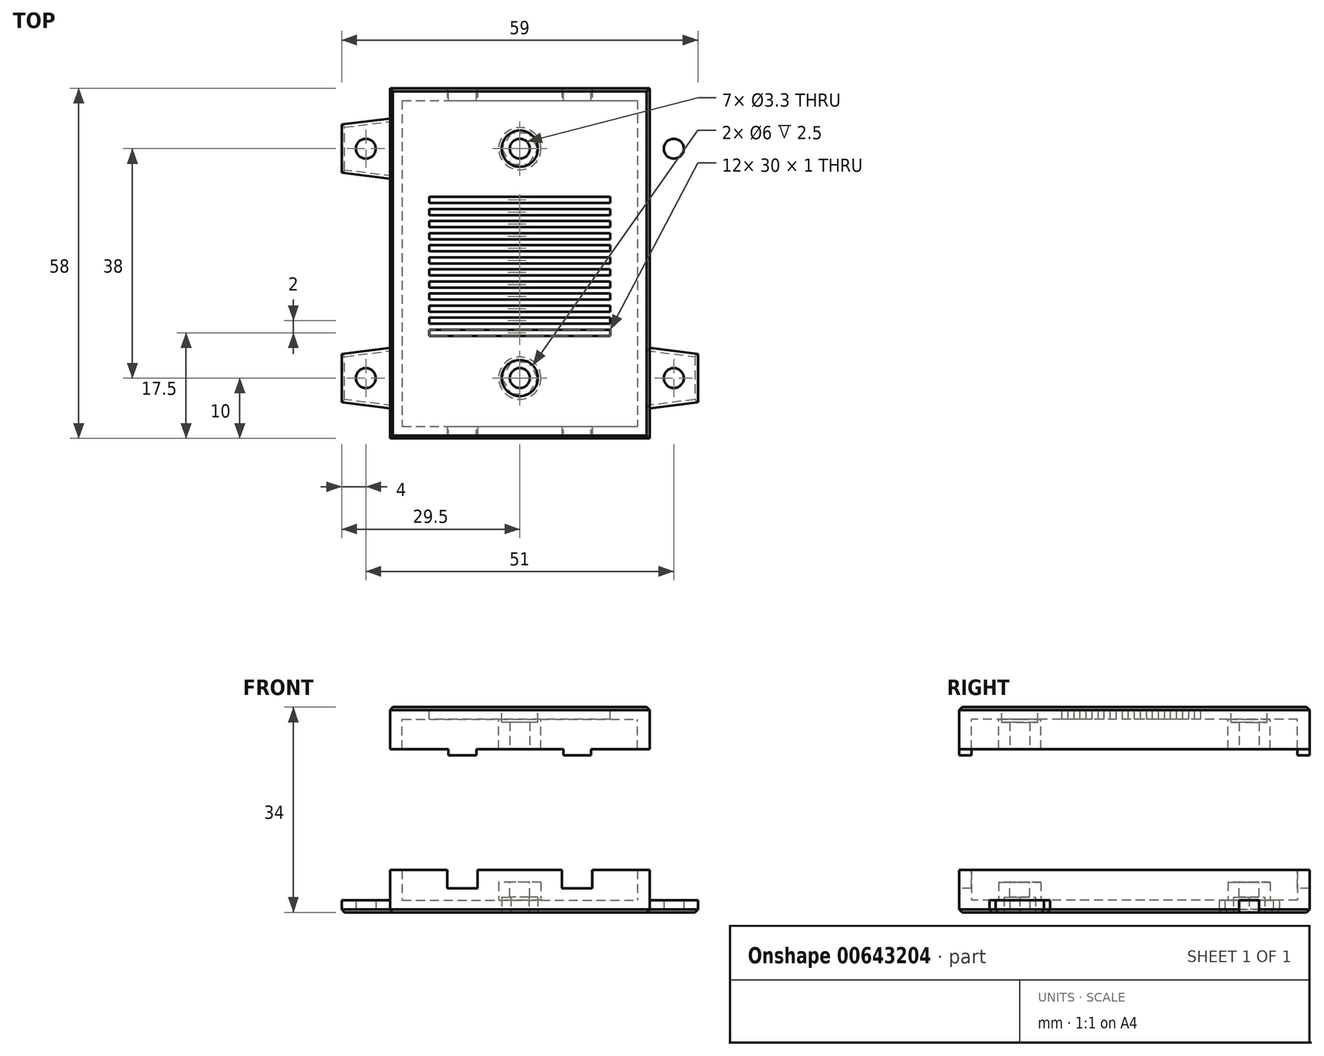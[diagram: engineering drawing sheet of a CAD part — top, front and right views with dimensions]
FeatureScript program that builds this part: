
annotation { "Feature Type Name" : "Feature", "Feature Type Description" : "" }
export const myFeature = defineFeature(function(context is Context, id is Id, definition is map)
    precondition{}
    {
        {
            var Q0;
            Q0=qCreatedBy(makeId("Top.planeOp"),FACE);
            var sketch = newSketch(context, id + "F0", { "sketchPlane" : qUnion([Q0])});
            skPoint(sketch, "E0", {"position": v(-9.5, 0) * mm});
            skPoint(sketch, "E1", {"position": v(0, -38) * mm});
            skPoint(sketch, "E2", {"position": v(0, 0) * mm});
            skPoint(sketch, "E3", {"position": v(9.5, 0) * mm});
            skLineSegment(sketch, "E4.bottom", {"start": v(-17.5, 6) * mm, "end": v(17.5, 6) * mm});
            skLineSegment(sketch, "E4.top", {"start": v(-17.5, -44) * mm, "end": v(17.5, -44) * mm});
            skLineSegment(sketch, "E4.left", {"start": v(-17.5, 6) * mm, "end": v(-17.5, -44) * mm});
            skLineSegment(sketch, "E4.right", {"start": v(17.5, 6) * mm, "end": v(17.5, -44) * mm});
            skPoint(sketch, "E5", {"position": v(-9.5, -38) * mm});
            skPoint(sketch, "E6", {"position": v(9.5, -38) * mm});
            skLineSegment(sketch, "E7.0", {"start": v(-19.5, -46) * mm, "end": v(19.5, -46) * mm});
            skLineSegment(sketch, "E7.1", {"start": v(-19.5, 8) * mm, "end": v(-19.5, -46) * mm});
            skLineSegment(sketch, "E7.2", {"start": v(-19.5, 8) * mm, "end": v(19.5, 8) * mm});
            skLineSegment(sketch, "E7.3", {"start": v(19.5, 8) * mm, "end": v(19.5, -46) * mm});
            skLineSegment(sketch, "E8.0", {"start": v(-21.5, -48) * mm, "end": v(21.5, -48) * mm});
            skLineSegment(sketch, "E8.1", {"start": v(-21.5, 10) * mm, "end": v(-21.5, -48) * mm});
            skLineSegment(sketch, "E8.2", {"start": v(-21.5, 10) * mm, "end": v(21.5, 10) * mm});
            skLineSegment(sketch, "E8.3", {"start": v(21.5, 10) * mm, "end": v(21.5, -48) * mm});
            skCircle(sketch, "E9", {"center": v(0, 0) * mm, "radius": 3.5 * mm});
            skCircle(sketch, "E10", {"center": v(0, -38) * mm, "radius": 3.5 * mm});
            skSolve(sketch);
        }
        {
            var Q0;
            Q0=makeQuery(id+"F0.imprint","IMPRINT",FACE,{"disambiguationData":[TD([[makeQuery(id+"F0.imprint","IMPRINT",EDGE,{"derivedFrom":sQuery(id+"F0.wireOp",EDGE,"E7.0")}),-1.0]])]});
            var Q1;
            Q1=makeQuery(id+"F0.imprint","IMPRINT",FACE,{"disambiguationData":[TD([[makeQuery(id+"F0.imprint","IMPRINT",EDGE,{"derivedFrom":sQuery(id+"F0.wireOp",EDGE,"E4.bottom")}),1.0]])]});
            var Q2;
            Q2=makeQuery(id+"F0.imprint","IMPRINT",FACE,{"disambiguationData":[TD([[makeQuery(id+"F0.imprint","IMPRINT",EDGE,{"derivedFrom":sQuery(id+"F0.wireOp",EDGE,"E4.bottom")}),-1.0]])]});
            var Q3;
            Q3=makeQuery(id+"F0.imprint","IMPRINT",FACE,{"disambiguationData":[TD([[makeQuery(id+"F0.imprint","IMPRINT",EDGE,{"derivedFrom":sQuery(id+"F0.wireOp",EDGE,"E9")}),1.0]])]});
            var Q4;
            Q4=makeQuery(id+"F0.imprint","IMPRINT",FACE,{"disambiguationData":[TD([[makeQuery(id+"F0.imprint","IMPRINT",EDGE,{"derivedFrom":sQuery(id+"F0.wireOp",EDGE,"E10")}),1.0]])]});
            extrude(context, id + "F1", {"entities" : qUnion([Q0, Q1, Q2, Q3, Q4]), "depth" : -2 * mm, "offsetDistance" : 25 * mm});
        }
        {
            var Q0;
            Q0=makeQuery(id+"F0.imprint","IMPRINT",FACE,{"disambiguationData":[TD([[makeQuery(id+"F0.imprint","IMPRINT",EDGE,{"derivedFrom":sQuery(id+"F0.wireOp",EDGE,"E7.0")}),-1.0]])]});
            extrude(context, id + "F2", {"entities" : qUnion([Q0]), "operationType" : NewBodyOperationType.ADD, "depth" : 5 * mm, "offsetDistance" : 25 * mm});
        }
        {
            var Q0;
            Q0=makeQuery(id+"F0.imprint","IMPRINT",FACE,{"disambiguationData":[TD([[makeQuery(id+"F0.imprint","IMPRINT",EDGE,{"derivedFrom":sQuery(id+"F0.wireOp",EDGE,"E9")}),1.0]])]});
            var Q1;
            Q1=makeQuery(id+"F0.imprint","IMPRINT",FACE,{"disambiguationData":[TD([[makeQuery(id+"F0.imprint","IMPRINT",EDGE,{"derivedFrom":sQuery(id+"F0.wireOp",EDGE,"E10")}),1.0]])]});
            extrude(context, id + "F3", {"entities" : qUnion([Q0, Q1]), "operationType" : NewBodyOperationType.ADD, "depth" : 3 * mm, "offsetDistance" : 25 * mm});
        }
        {
            var Q0;
            Q0=makeQuery(id+"F3.opExtrude","CAP_FACE",FACE,{"disambiguationData":[OSD([sQuery(id+"F0.wireOp",EDGE,"E9")])],"isStart":false});
            var sketch = newSketch(context, id + "F4", { "sketchPlane" : qUnion([Q0])});
            skPoint(sketch, "E11", {"position": v(0, 0) * mm});
            skCircle(sketch, "E12.0", {"center": v(0, -38) * mm, "radius": 3.5 * mm});
            skCircle(sketch, "E13.0", {"center": v(0, 0) * mm, "radius": 3.5 * mm});
            skSolve(sketch);
        }
        {
            var Q0;
            Q0=sQuery(id+"F4.wireOp",VERTEX,"E12.0.center");
            var Q1;
            Q1=sQuery(id+"F4.wireOp",VERTEX,"E11");
            var Q2;
            Q2=makeQuery(id+"F1.opExtrude","SWEPT_BODY",BODY,{"disambiguationData":[OSD([sQuery(id+"F0.wireOp",EDGE,"E8.0"),sQuery(id+"F0.wireOp",EDGE,"E8.1"),sQuery(id+"F0.wireOp",EDGE,"E8.2"),sQuery(id+"F0.wireOp",EDGE,"E8.3")])]});
            hole(context, id + "F5", {"style" : HoleStyle.SIMPLE, "endStyle" : HoleEndStyle.THROUGH, "standardTappedOrClearance" : lookupTablePath({ "standard" : "ISO", "fit" : "Normal", "size" : "M3", "type" : "Clearance" }), "standardBlindInLast" : lookupTablePath({ "fit" : "Standard", "standard" : "ISO", "size" : "M3", "type" : "Clearance" }), "holeDiameter" : 3.3 * mm, "majorDiameter" : 3 * mm, "isTappedThrough" : true, "tappedDepth" : 12 * mm, "tapClearance" : 3, "locations" : qUnion([Q0, Q1]), "scope" : qUnion([Q2])});
        }
        {
            var Q0;
            Q0=makeQuery(id+"F2.opExtrude","CAP_FACE",FACE,{"disambiguationData":[OSD([sQuery(id+"F0.wireOp",EDGE,"E7.0"),sQuery(id+"F0.wireOp",EDGE,"E7.1"),sQuery(id+"F0.wireOp",EDGE,"E7.2"),sQuery(id+"F0.wireOp",EDGE,"E7.3"),sQuery(id+"F0.wireOp",EDGE,"E8.0"),sQuery(id+"F0.wireOp",EDGE,"E8.1"),sQuery(id+"F0.wireOp",EDGE,"E8.2"),sQuery(id+"F0.wireOp",EDGE,"E8.3")])],"isStart":false});
            var sketch = newSketch(context, id + "F6", { "sketchPlane" : qUnion([Q0])});
            skLineSegment(sketch, "E14", {"start": v(-12, 10) * mm, "end": v(-12, -48) * mm});
            skLineSegment(sketch, "E15", {"start": v(-7, 10) * mm, "end": v(-7, -48) * mm});
            skLineSegment(sketch, "E16", {"start": v(7, 10) * mm, "end": v(7, -48) * mm});
            skLineSegment(sketch, "E17", {"start": v(12, 10) * mm, "end": v(12, -48) * mm});
            skSolve(sketch);
        }
        {
            var Q0;
            {var subQ0=sQuery(id+"F6.wireOp",EDGE,"E16");var subQ1=makeQuery(id+"F2.opExtrude","CAP_EDGE",EDGE,{"disambiguationData":[OSD([sQuery(id+"F0.wireOp",EDGE,"E8.0")])],"isStart":false});var subQ2=makeQuery(id+"F6.imprint","INTERSECT",VERTEX,{"derivedFrom":[subQ1,subQ0]});Q0=makeQuery(id+"F6.imprint","IMPRINT",FACE,{"disambiguationData":[TD([[makeQuery(id+"F6.imprint","IMPRINT",EDGE,{"disambiguationData":[TD([[subQ2,1.0]])],"derivedFrom":subQ0}),1.0]])]});}
            var Q1;
            {var subQ0=sQuery(id+"F6.wireOp",EDGE,"E14");var subQ1=makeQuery(id+"F2.opExtrude","CAP_EDGE",EDGE,{"disambiguationData":[OSD([sQuery(id+"F0.wireOp",EDGE,"E8.0")])],"isStart":false});var subQ2=makeQuery(id+"F6.imprint","INTERSECT",VERTEX,{"derivedFrom":[subQ1,subQ0]});Q1=makeQuery(id+"F6.imprint","IMPRINT",FACE,{"disambiguationData":[TD([[makeQuery(id+"F6.imprint","IMPRINT",EDGE,{"disambiguationData":[TD([[subQ2,1.0]])],"derivedFrom":subQ0}),1.0]])]});}
            var Q2;
            {var subQ0=sQuery(id+"F6.wireOp",EDGE,"E14");var subQ1=makeQuery(id+"F2.opExtrude","CAP_EDGE",EDGE,{"disambiguationData":[OSD([sQuery(id+"F0.wireOp",EDGE,"E8.2")])],"isStart":false});var subQ2=makeQuery(id+"F6.imprint","INTERSECT",VERTEX,{"derivedFrom":[subQ1,subQ0]});Q2=makeQuery(id+"F6.imprint","IMPRINT",FACE,{"disambiguationData":[TD([[makeQuery(id+"F6.imprint","IMPRINT",EDGE,{"disambiguationData":[TD([[subQ2,-1.0]])],"derivedFrom":subQ0}),1.0]])]});}
            var Q3;
            {var subQ0=sQuery(id+"F6.wireOp",EDGE,"E16");var subQ1=makeQuery(id+"F2.opExtrude","CAP_EDGE",EDGE,{"disambiguationData":[OSD([sQuery(id+"F0.wireOp",EDGE,"E8.2")])],"isStart":false});var subQ2=makeQuery(id+"F6.imprint","INTERSECT",VERTEX,{"derivedFrom":[subQ1,subQ0]});Q3=makeQuery(id+"F6.imprint","IMPRINT",FACE,{"disambiguationData":[TD([[makeQuery(id+"F6.imprint","IMPRINT",EDGE,{"disambiguationData":[TD([[subQ2,-1.0]])],"derivedFrom":subQ0}),1.0]])]});}
            extrude(context, id + "F7", {"entities" : qUnion([Q0, Q1, Q2, Q3]), "operationType" : NewBodyOperationType.REMOVE, "oppositeDirection" : true, "depth" : 3 * mm, "offsetDistance" : 25 * mm});
        }
        {
            var Q0;
            {var subQ0=sQuery(id+"F0.wireOp",EDGE,"E8.2");var subQ2=sQuery(id+"F0.wireOp",EDGE,"E7.2");var subQ3=sQuery(id+"F0.wireOp",EDGE,"E8.0");var subQ4=sQuery(id+"F0.wireOp",EDGE,"E7.0");var subQ5=sQuery(id+"F0.wireOp",EDGE,"E7.1");var subQ6=sQuery(id+"F0.wireOp",EDGE,"E8.1");Q0=makeQuery(id+"F7.boolean.opBoolean","SPLIT",FACE,{"disambiguationData":[TD([makeQuery(id+"F1.opExtrude","SWEPT_FACE",FACE,{"disambiguationData":[OSD([subQ6])]})])],"derivedFrom":makeQuery(id+"F2.opExtrude","CAP_FACE",FACE,{"disambiguationData":[OSD([subQ4,subQ5,subQ2,sQuery(id+"F0.wireOp",EDGE,"E7.3"),subQ3,subQ6,subQ0,sQuery(id+"F0.wireOp",EDGE,"E8.3")])],"isStart":false})});}
            cPlane(context, id + "F8", {"entities" : qUnion([Q0]), "cplaneType" : CPlaneType.OFFSET, "offset" : 25 * mm, "width" : 150 * mm, "height" : 150 * mm});
        }
        {
            var Q0;
            Q0=qCreatedBy(id+"F8.planeOp",FACE);
            var sketch = newSketch(context, id + "F9", { "sketchPlane" : qUnion([Q0])});
            skLineSegment(sketch, "E18.0", {"start": v(-21.5, 10) * mm, "end": v(-21.5, -48) * mm});
            skLineSegment(sketch, "E19.0", {"start": v(-21.5, 10) * mm, "end": v(21.5, 10) * mm});
            skLineSegment(sketch, "E20.0", {"start": v(21.5, 10) * mm, "end": v(21.5, -48) * mm});
            skLineSegment(sketch, "E21.0", {"start": v(-21.5, -48) * mm, "end": v(21.5, -48) * mm});
            skLineSegment(sketch, "E22.0", {"start": v(-19.5, -46) * mm, "end": v(19.5, -46) * mm});
            skLineSegment(sketch, "E23.0", {"start": v(19.5, 8) * mm, "end": v(19.5, -46) * mm});
            skLineSegment(sketch, "E24.0", {"start": v(-19.5, 8) * mm, "end": v(-19.5, -46) * mm});
            skLineSegment(sketch, "E25.0", {"start": v(-19.5, 8) * mm, "end": v(19.5, 8) * mm});
            skLineSegment(sketch, "E26.0", {"start": v(-7, 10) * mm, "end": v(-7, 8) * mm});
            skLineSegment(sketch, "E27.0", {"start": v(-12, 10) * mm, "end": v(-12, 8) * mm});
            skLineSegment(sketch, "E28.0", {"start": v(12, 10) * mm, "end": v(12, 8) * mm});
            skLineSegment(sketch, "E29.0", {"start": v(7, 10) * mm, "end": v(7, 8) * mm});
            skCircle(sketch, "E30.0", {"center": v(0, 0) * mm, "radius": 3.5 * mm});
            skCircle(sketch, "E31.0", {"center": v(0, -38) * mm, "radius": 3.5 * mm});
            skLineSegment(sketch, "E32.0", {"start": v(7, -46) * mm, "end": v(7, -48) * mm});
            skLineSegment(sketch, "E33.0", {"start": v(12, -46) * mm, "end": v(12, -48) * mm});
            skLineSegment(sketch, "E34.0", {"start": v(-7, -46) * mm, "end": v(-7, -48) * mm});
            skLineSegment(sketch, "E35.0", {"start": v(-12, -46) * mm, "end": v(-12, -48) * mm});
            skSolve(sketch);
        }
        {
            var Q0;
            {var subQ5=sQuery(id+"F9.wireOp",EDGE,"E23.0");Q0=makeQuery(id+"F9.imprint","IMPRINT",FACE,{"disambiguationData":[TD([[makeQuery(id+"F9.imprint","IMPRINT",EDGE,{"derivedFrom":subQ5}),-1.0]])]});}
            var Q1;
            Q1=makeQuery(id+"F9.imprint","IMPRINT",FACE,{"disambiguationData":[TD([[makeQuery(id+"F9.imprint","IMPRINT",EDGE,{"derivedFrom":sQuery(id+"F9.wireOp",EDGE,"E31.0")}),1.0]])]});
            var Q2;
            Q2=makeQuery(id+"F9.imprint","IMPRINT",FACE,{"disambiguationData":[TD([[makeQuery(id+"F9.imprint","IMPRINT",EDGE,{"derivedFrom":sQuery(id+"F9.wireOp",EDGE,"E30.0")}),1.0]])]});
            var Q3;
            {var subQ0=sQuery(id+"F9.wireOp",EDGE,"E32.0");Q3=makeQuery(id+"F9.imprint","IMPRINT",FACE,{"disambiguationData":[TD([[makeQuery(id+"F9.imprint","IMPRINT",EDGE,{"derivedFrom":subQ0}),-1.0]])]});}
            var Q4;
            {var subQ0=sQuery(id+"F9.wireOp",EDGE,"E34.0");Q4=makeQuery(id+"F9.imprint","IMPRINT",FACE,{"disambiguationData":[TD([[makeQuery(id+"F9.imprint","IMPRINT",EDGE,{"derivedFrom":subQ0}),-1.0]])]});}
            var Q5;
            {var subQ4=sQuery(id+"F9.wireOp",EDGE,"E18.0");Q5=makeQuery(id+"F9.imprint","IMPRINT",FACE,{"disambiguationData":[TD([[makeQuery(id+"F9.imprint","IMPRINT",EDGE,{"derivedFrom":subQ4}),1.0]])]});}
            var Q6;
            {var subQ0=sQuery(id+"F9.wireOp",EDGE,"E32.0");Q6=makeQuery(id+"F9.imprint","IMPRINT",FACE,{"disambiguationData":[TD([[makeQuery(id+"F9.imprint","IMPRINT",EDGE,{"derivedFrom":subQ0}),1.0]])]});}
            var Q7;
            {var subQ3=sQuery(id+"F9.wireOp",EDGE,"E20.0");Q7=makeQuery(id+"F9.imprint","IMPRINT",FACE,{"disambiguationData":[TD([[makeQuery(id+"F9.imprint","IMPRINT",EDGE,{"derivedFrom":subQ3}),-1.0]])]});}
            var Q8;
            {var subQ0=sQuery(id+"F9.wireOp",EDGE,"E28.0");Q8=makeQuery(id+"F9.imprint","IMPRINT",FACE,{"disambiguationData":[TD([[makeQuery(id+"F9.imprint","IMPRINT",EDGE,{"derivedFrom":subQ0}),-1.0]])]});}
            var Q9;
            {var subQ0=sQuery(id+"F9.wireOp",EDGE,"E26.0");Q9=makeQuery(id+"F9.imprint","IMPRINT",FACE,{"disambiguationData":[TD([[makeQuery(id+"F9.imprint","IMPRINT",EDGE,{"derivedFrom":subQ0}),1.0]])]});}
            var Q10;
            {var subQ0=sQuery(id+"F9.wireOp",EDGE,"E26.0");Q10=makeQuery(id+"F9.imprint","IMPRINT",FACE,{"disambiguationData":[TD([[makeQuery(id+"F9.imprint","IMPRINT",EDGE,{"derivedFrom":subQ0}),-1.0]])]});}
            extrude(context, id + "F10", {"entities" : qUnion([Q0, Q1, Q2, Q3, Q4, Q5, Q6, Q7, Q8, Q9, Q10]), "depth" : 2 * mm, "offsetDistance" : 25 * mm});
        }
        {
            var Q0;
            {var subQ3=sQuery(id+"F9.wireOp",EDGE,"E20.0");Q0=makeQuery(id+"F9.imprint","IMPRINT",FACE,{"disambiguationData":[TD([[makeQuery(id+"F9.imprint","IMPRINT",EDGE,{"derivedFrom":subQ3}),-1.0]])]});}
            var Q1;
            {var subQ0=sQuery(id+"F9.wireOp",EDGE,"E32.0");Q1=makeQuery(id+"F9.imprint","IMPRINT",FACE,{"disambiguationData":[TD([[makeQuery(id+"F9.imprint","IMPRINT",EDGE,{"derivedFrom":subQ0}),1.0]])]});}
            var Q2;
            {var subQ0=sQuery(id+"F9.wireOp",EDGE,"E32.0");Q2=makeQuery(id+"F9.imprint","IMPRINT",FACE,{"disambiguationData":[TD([[makeQuery(id+"F9.imprint","IMPRINT",EDGE,{"derivedFrom":subQ0}),-1.0]])]});}
            var Q3;
            {var subQ0=sQuery(id+"F9.wireOp",EDGE,"E34.0");Q3=makeQuery(id+"F9.imprint","IMPRINT",FACE,{"disambiguationData":[TD([[makeQuery(id+"F9.imprint","IMPRINT",EDGE,{"derivedFrom":subQ0}),-1.0]])]});}
            var Q4;
            {var subQ4=sQuery(id+"F9.wireOp",EDGE,"E18.0");Q4=makeQuery(id+"F9.imprint","IMPRINT",FACE,{"disambiguationData":[TD([[makeQuery(id+"F9.imprint","IMPRINT",EDGE,{"derivedFrom":subQ4}),1.0]])]});}
            var Q5;
            {var subQ0=sQuery(id+"F9.wireOp",EDGE,"E26.0");Q5=makeQuery(id+"F9.imprint","IMPRINT",FACE,{"disambiguationData":[TD([[makeQuery(id+"F9.imprint","IMPRINT",EDGE,{"derivedFrom":subQ0}),-1.0]])]});}
            var Q6;
            {var subQ0=sQuery(id+"F9.wireOp",EDGE,"E26.0");Q6=makeQuery(id+"F9.imprint","IMPRINT",FACE,{"disambiguationData":[TD([[makeQuery(id+"F9.imprint","IMPRINT",EDGE,{"derivedFrom":subQ0}),1.0]])]});}
            var Q7;
            {var subQ0=sQuery(id+"F9.wireOp",EDGE,"E28.0");Q7=makeQuery(id+"F9.imprint","IMPRINT",FACE,{"disambiguationData":[TD([[makeQuery(id+"F9.imprint","IMPRINT",EDGE,{"derivedFrom":subQ0}),-1.0]])]});}
            var Q8;
            Q8=makeQuery(id+"F9.imprint","IMPRINT",FACE,{"disambiguationData":[TD([[makeQuery(id+"F9.imprint","IMPRINT",EDGE,{"derivedFrom":sQuery(id+"F9.wireOp",EDGE,"E30.0")}),1.0]])]});
            var Q9;
            Q9=makeQuery(id+"F9.imprint","IMPRINT",FACE,{"disambiguationData":[TD([[makeQuery(id+"F9.imprint","IMPRINT",EDGE,{"derivedFrom":sQuery(id+"F9.wireOp",EDGE,"E31.0")}),1.0]])]});
            extrude(context, id + "F11", {"entities" : qUnion([Q0, Q1, Q2, Q3, Q4, Q5, Q6, Q7, Q8, Q9]), "operationType" : NewBodyOperationType.ADD, "oppositeDirection" : true, "depth" : 5 * mm, "offsetDistance" : 25 * mm});
        }
        {
            var Q0;
            Q0=makeQuery(id+"F11.opExtrude","CAP_FACE",FACE,{"disambiguationData":[OSD([sQuery(id+"F9.wireOp",EDGE,"E18.0"),sQuery(id+"F9.wireOp",EDGE,"E19.0"),sQuery(id+"F9.wireOp",EDGE,"E20.0"),sQuery(id+"F9.wireOp",EDGE,"E21.0"),sQuery(id+"F9.wireOp",EDGE,"E22.0"),sQuery(id+"F9.wireOp",EDGE,"E23.0"),sQuery(id+"F9.wireOp",EDGE,"E24.0"),sQuery(id+"F9.wireOp",EDGE,"E25.0")])],"isStart":false});
            var sketch = newSketch(context, id + "F12", { "sketchPlane" : qUnion([Q0])});
            skLineSegment(sketch, "E36.0", {"start": v(-12, -10) * mm, "end": v(-12, -8) * mm});
            skLineSegment(sketch, "E37.0", {"start": v(-7, -10) * mm, "end": v(-7, -8) * mm});
            skLineSegment(sketch, "E38.0", {"start": v(7, -10) * mm, "end": v(7, -8) * mm});
            skLineSegment(sketch, "E39.0", {"start": v(12, -10) * mm, "end": v(12, -8) * mm});
            skLineSegment(sketch, "E40.0", {"start": v(-12, 46) * mm, "end": v(-12, 48) * mm});
            skLineSegment(sketch, "E41.0", {"start": v(-7, 46) * mm, "end": v(-7, 48) * mm});
            skLineSegment(sketch, "E42.0", {"start": v(7, 46) * mm, "end": v(7, 48) * mm});
            skLineSegment(sketch, "E43.0", {"start": v(12, 46) * mm, "end": v(12, 48) * mm});
            skLineSegment(sketch, "E44", {"start": v(-11.8, 48) * mm, "end": v(-11.8, 46) * mm});
            skLineSegment(sketch, "E45", {"start": v(-7.2, 48) * mm, "end": v(-7.2, 46) * mm});
            skLineSegment(sketch, "E46", {"start": v(7.2, 48) * mm, "end": v(7.2, 46) * mm});
            skLineSegment(sketch, "E47", {"start": v(11.8, 48) * mm, "end": v(11.8, 46) * mm});
            skLineSegment(sketch, "E48", {"start": v(-11.8, -8) * mm, "end": v(-11.8, -10) * mm});
            skLineSegment(sketch, "E49", {"start": v(-7.2, -8) * mm, "end": v(-7.2, -10) * mm});
            skLineSegment(sketch, "E50", {"start": v(7.2, -8) * mm, "end": v(7.2, -10) * mm});
            skLineSegment(sketch, "E51", {"start": v(11.8, -8) * mm, "end": v(11.8, -10) * mm});
            skCircle(sketch, "E52.0", {"center": v(0, 0) * mm, "radius": 3.5 * mm});
            skCircle(sketch, "E53.0", {"center": v(0, 38) * mm, "radius": 3.5 * mm});
            skSolve(sketch);
        }
        {
            var Q0;
            {var subQ0=sQuery(id+"F12.wireOp",EDGE,"E44");Q0=makeQuery(id+"F12.imprint","IMPRINT",FACE,{"disambiguationData":[TD([[makeQuery(id+"F12.imprint","IMPRINT",EDGE,{"derivedFrom":subQ0}),1.0]])]});}
            var Q1;
            {var subQ0=sQuery(id+"F12.wireOp",EDGE,"E46");Q1=makeQuery(id+"F12.imprint","IMPRINT",FACE,{"disambiguationData":[TD([[makeQuery(id+"F12.imprint","IMPRINT",EDGE,{"derivedFrom":subQ0}),1.0]])]});}
            var Q2;
            {var subQ0=sQuery(id+"F12.wireOp",EDGE,"E48");Q2=makeQuery(id+"F12.imprint","IMPRINT",FACE,{"disambiguationData":[TD([[makeQuery(id+"F12.imprint","IMPRINT",EDGE,{"derivedFrom":subQ0}),1.0]])]});}
            var Q3;
            {var subQ0=sQuery(id+"F12.wireOp",EDGE,"E50");Q3=makeQuery(id+"F12.imprint","IMPRINT",FACE,{"disambiguationData":[TD([[makeQuery(id+"F12.imprint","IMPRINT",EDGE,{"derivedFrom":subQ0}),1.0]])]});}
            extrude(context, id + "F13", {"entities" : qUnion([Q0, Q1, Q2, Q3]), "operationType" : NewBodyOperationType.ADD, "depth" : 1 * mm, "offsetDistance" : 25 * mm});
        }
        {
            var Q0;
            Q0=sQuery(id+"F12.wireOp",VERTEX,"E53.0.center");
            var Q1;
            Q1=sQuery(id+"F12.wireOp",VERTEX,"E52.0.center");
            var Q2;
            Q2=makeQuery(id+"F10.opExtrude","SWEPT_BODY",BODY,{"disambiguationData":[OSD([sQuery(id+"F9.wireOp",EDGE,"E18.0"),sQuery(id+"F9.wireOp",EDGE,"E19.0"),sQuery(id+"F9.wireOp",EDGE,"E20.0"),sQuery(id+"F9.wireOp",EDGE,"E21.0")])]});
            hole(context, id + "F14", {"style" : HoleStyle.SIMPLE, "endStyle" : HoleEndStyle.THROUGH, "standardTappedOrClearance" : lookupTablePath({ "standard" : "ISO", "fit" : "Normal", "size" : "M3", "type" : "Clearance" }), "standardBlindInLast" : lookupTablePath({ "fit" : "Standard", "standard" : "ISO", "size" : "M3", "type" : "Clearance" }), "holeDiameter" : 3.3 * mm, "majorDiameter" : 5 * mm, "isTappedThrough" : true, "tappedDepth" : 12 * mm, "tapClearance" : 3, "locations" : qUnion([Q0, Q1]), "scope" : qUnion([Q2])});
        }
        {
            var Q0;
            Q0=makeQuery(id+"F10.opExtrude","CAP_FACE",FACE,{"disambiguationData":[OSD([sQuery(id+"F9.wireOp",EDGE,"E18.0"),sQuery(id+"F9.wireOp",EDGE,"E19.0"),sQuery(id+"F9.wireOp",EDGE,"E20.0"),sQuery(id+"F9.wireOp",EDGE,"E21.0")])],"isStart":false});
            var sketch = newSketch(context, id + "F15", { "sketchPlane" : qUnion([Q0])});
            skCircle(sketch, "E54", {"center": v(0, 0) * mm, "radius": 3 * mm});
            skCircle(sketch, "E55", {"center": v(0, -38) * mm, "radius": 3 * mm});
            skSolve(sketch);
        }
        {
            var Q0;
            Q0=makeQuery(id+"F15.imprint","IMPRINT",FACE,{"disambiguationData":[TD([[makeQuery(id+"F15.imprint","IMPRINT",EDGE,{"derivedFrom":sQuery(id+"F15.wireOp",EDGE,"E55")}),1.0]])]});
            var Q1;
            Q1=makeQuery(id+"F15.imprint","IMPRINT",FACE,{"disambiguationData":[TD([[makeQuery(id+"F15.imprint","IMPRINT",EDGE,{"derivedFrom":sQuery(id+"F15.wireOp",EDGE,"E54")}),1.0]])]});
            extrude(context, id + "F16", {"entities" : qUnion([Q0, Q1]), "operationType" : NewBodyOperationType.REMOVE, "oppositeDirection" : true, "depth" : 2.5 * mm, "offsetDistance" : 25 * mm});
        }
        {
            var Q0;
            Q0=makeQuery(id+"F1.opExtrude","CAP_FACE",FACE,{"disambiguationData":[OSD([sQuery(id+"F0.wireOp",EDGE,"E8.0"),sQuery(id+"F0.wireOp",EDGE,"E8.1"),sQuery(id+"F0.wireOp",EDGE,"E8.2"),sQuery(id+"F0.wireOp",EDGE,"E8.3")])],"isStart":false});
            var sketch = newSketch(context, id + "F17", { "sketchPlane" : qUnion([Q0])});
            skCircle(sketch, "E56.cCircle", {"center": v(0, 0) * mm, "radius": 2.6 * mm, "construction": true});
            skLineSegment(sketch, "E56.0", {"start": v(1.5, -2.6) * mm, "end": v(-1.5, -2.6) * mm});
            skLineSegment(sketch, "E56.1", {"start": v(-1.5, -2.6) * mm, "end": v(-3, 0) * mm});
            skLineSegment(sketch, "E56.2", {"start": v(-3, 0) * mm, "end": v(-1.5, 2.6) * mm});
            skLineSegment(sketch, "E56.3", {"start": v(-1.5, 2.6) * mm, "end": v(1.5, 2.6) * mm});
            skLineSegment(sketch, "E56.4", {"start": v(1.5, 2.6) * mm, "end": v(3, 0) * mm});
            skLineSegment(sketch, "E56.5", {"start": v(3, 0) * mm, "end": v(1.5, -2.6) * mm});
            skPoint(sketch, "E56.0.midPoint", {"position": v(0, -2.6) * mm});
            skCircle(sketch, "E57.cCircle", {"center": v(0, 38) * mm, "radius": 2.6 * mm, "construction": true});
            skLineSegment(sketch, "E57.0", {"start": v(1.5, 35.4) * mm, "end": v(-1.5, 35.4) * mm});
            skLineSegment(sketch, "E57.1", {"start": v(-1.5, 35.4) * mm, "end": v(-3, 38) * mm});
            skLineSegment(sketch, "E57.2", {"start": v(-3, 38) * mm, "end": v(-1.5, 40.6) * mm});
            skLineSegment(sketch, "E57.3", {"start": v(-1.5, 40.6) * mm, "end": v(1.5, 40.6) * mm});
            skLineSegment(sketch, "E57.4", {"start": v(1.5, 40.6) * mm, "end": v(3, 38) * mm});
            skLineSegment(sketch, "E57.5", {"start": v(3, 38) * mm, "end": v(1.5, 35.4) * mm});
            skPoint(sketch, "E57.0.midPoint", {"position": v(0, 35.4) * mm});
            skSolve(sketch);
        }
        {
            var Q0;
            Q0=makeQuery(id+"F17.imprint","IMPRINT",FACE,{"disambiguationData":[TD([[makeQuery(id+"F17.imprint","IMPRINT",EDGE,{"derivedFrom":sQuery(id+"F17.wireOp",EDGE,"E57.0")}),-1.0]])]});
            var Q1;
            Q1=makeQuery(id+"F17.imprint","IMPRINT",FACE,{"disambiguationData":[TD([[makeQuery(id+"F17.imprint","IMPRINT",EDGE,{"derivedFrom":sQuery(id+"F17.wireOp",EDGE,"E56.0")}),-1.0]])]});
            extrude(context, id + "F18", {"entities" : qUnion([Q0, Q1]), "operationType" : NewBodyOperationType.REMOVE, "oppositeDirection" : true, "depth" : 2.5 * mm, "offsetDistance" : 25 * mm});
        }
        {
            var Q0;
            Q0=makeQuery(id+"F10.opExtrude","CAP_FACE",FACE,{"disambiguationData":[OSD([sQuery(id+"F9.wireOp",EDGE,"E18.0"),sQuery(id+"F9.wireOp",EDGE,"E19.0"),sQuery(id+"F9.wireOp",EDGE,"E20.0"),sQuery(id+"F9.wireOp",EDGE,"E21.0")])],"isStart":false});
            var sketch = newSketch(context, id + "F19", { "sketchPlane" : qUnion([Q0])});
            skLineSegment(sketch, "E58", {"start": v(0, 0) * mm, "end": v(0, -38) * mm, "construction": true});
            skLineSegment(sketch, "E59.bottom", {"start": v(-15, -9) * mm, "end": v(15, -9) * mm});
            skLineSegment(sketch, "E59.top", {"start": v(-15, -8) * mm, "end": v(15, -8) * mm});
            skLineSegment(sketch, "E59.left", {"start": v(-15, -9) * mm, "end": v(-15, -8) * mm});
            skLineSegment(sketch, "E59.right", {"start": v(15, -9) * mm, "end": v(15, -8) * mm});
            skPoint(sketch, "E60", {"position": v(0, -8) * mm});
            skLineSegment(sketch, "E61.1.0.0", {"start": v(-15, -11) * mm, "end": v(15, -11) * mm});
            skLineSegment(sketch, "E61.1.0.1", {"start": v(15, -11) * mm, "end": v(15, -10) * mm});
            skLineSegment(sketch, "E61.1.0.2", {"start": v(-15, -10) * mm, "end": v(15, -10) * mm});
            skLineSegment(sketch, "E61.1.0.3", {"start": v(-15, -11) * mm, "end": v(-15, -10) * mm});
            skLineSegment(sketch, "E61.2.0.0", {"start": v(-15, -13) * mm, "end": v(15, -13) * mm});
            skLineSegment(sketch, "E61.2.0.1", {"start": v(15, -13) * mm, "end": v(15, -12) * mm});
            skLineSegment(sketch, "E61.2.0.2", {"start": v(-15, -12) * mm, "end": v(15, -12) * mm});
            skLineSegment(sketch, "E61.2.0.3", {"start": v(-15, -13) * mm, "end": v(-15, -12) * mm});
            skLineSegment(sketch, "E61.direction1", {"start": v(-15, -9) * mm, "end": v(-15, -11) * mm, "construction": true});
            skLineSegment(sketch, "E62.0.3.0", {"start": v(-15, -15) * mm, "end": v(15, -15) * mm});
            skLineSegment(sketch, "E62.3.3.0", {"start": v(15, -15) * mm, "end": v(15, -14) * mm});
            skLineSegment(sketch, "E62.6.3.0", {"start": v(-15, -14) * mm, "end": v(15, -14) * mm});
            skLineSegment(sketch, "E62.9.3.0", {"start": v(-15, -15) * mm, "end": v(-15, -14) * mm});
            skLineSegment(sketch, "E62.0.4.0", {"start": v(-15, -17) * mm, "end": v(15, -17) * mm});
            skLineSegment(sketch, "E62.3.4.0", {"start": v(15, -17) * mm, "end": v(15, -16) * mm});
            skLineSegment(sketch, "E62.6.4.0", {"start": v(-15, -16) * mm, "end": v(15, -16) * mm});
            skLineSegment(sketch, "E62.9.4.0", {"start": v(-15, -17) * mm, "end": v(-15, -16) * mm});
            skLineSegment(sketch, "E62.0.5.0", {"start": v(-15, -19) * mm, "end": v(15, -19) * mm});
            skLineSegment(sketch, "E62.3.5.0", {"start": v(15, -19) * mm, "end": v(15, -18) * mm});
            skLineSegment(sketch, "E62.6.5.0", {"start": v(-15, -18) * mm, "end": v(15, -18) * mm});
            skLineSegment(sketch, "E62.9.5.0", {"start": v(-15, -19) * mm, "end": v(-15, -18) * mm});
            skLineSegment(sketch, "E62.0.6.0", {"start": v(-15, -21) * mm, "end": v(15, -21) * mm});
            skLineSegment(sketch, "E62.3.6.0", {"start": v(15, -21) * mm, "end": v(15, -20) * mm});
            skLineSegment(sketch, "E62.6.6.0", {"start": v(-15, -20) * mm, "end": v(15, -20) * mm});
            skLineSegment(sketch, "E62.9.6.0", {"start": v(-15, -21) * mm, "end": v(-15, -20) * mm});
            skLineSegment(sketch, "E62.0.7.0", {"start": v(-15, -23) * mm, "end": v(15, -23) * mm});
            skLineSegment(sketch, "E62.3.7.0", {"start": v(15, -23) * mm, "end": v(15, -22) * mm});
            skLineSegment(sketch, "E62.6.7.0", {"start": v(-15, -22) * mm, "end": v(15, -22) * mm});
            skLineSegment(sketch, "E62.9.7.0", {"start": v(-15, -23) * mm, "end": v(-15, -22) * mm});
            skLineSegment(sketch, "E62.0.8.0", {"start": v(-15, -25) * mm, "end": v(15, -25) * mm});
            skLineSegment(sketch, "E62.3.8.0", {"start": v(15, -25) * mm, "end": v(15, -24) * mm});
            skLineSegment(sketch, "E62.6.8.0", {"start": v(-15, -24) * mm, "end": v(15, -24) * mm});
            skLineSegment(sketch, "E62.9.8.0", {"start": v(-15, -25) * mm, "end": v(-15, -24) * mm});
            skLineSegment(sketch, "E62.0.9.0", {"start": v(-15, -27) * mm, "end": v(15, -27) * mm});
            skLineSegment(sketch, "E62.3.9.0", {"start": v(15, -27) * mm, "end": v(15, -26) * mm});
            skLineSegment(sketch, "E62.6.9.0", {"start": v(-15, -26) * mm, "end": v(15, -26) * mm});
            skLineSegment(sketch, "E62.9.9.0", {"start": v(-15, -27) * mm, "end": v(-15, -26) * mm});
            skLineSegment(sketch, "E62.0.10.0", {"start": v(-15, -29) * mm, "end": v(15, -29) * mm});
            skLineSegment(sketch, "E62.3.10.0", {"start": v(15, -29) * mm, "end": v(15, -28) * mm});
            skLineSegment(sketch, "E62.6.10.0", {"start": v(-15, -28) * mm, "end": v(15, -28) * mm});
            skLineSegment(sketch, "E62.9.10.0", {"start": v(-15, -29) * mm, "end": v(-15, -28) * mm});
            skLineSegment(sketch, "E62.0.11.0", {"start": v(-15, -31) * mm, "end": v(15, -31) * mm});
            skLineSegment(sketch, "E62.3.11.0", {"start": v(15, -31) * mm, "end": v(15, -30) * mm});
            skLineSegment(sketch, "E62.6.11.0", {"start": v(-15, -30) * mm, "end": v(15, -30) * mm});
            skLineSegment(sketch, "E62.9.11.0", {"start": v(-15, -31) * mm, "end": v(-15, -30) * mm});
            skSolve(sketch);
        }
        {
            var Q0;
            Q0=makeQuery(id+"F19.imprint","IMPRINT",FACE,{"disambiguationData":[TD([[makeQuery(id+"F19.imprint","IMPRINT",EDGE,{"derivedFrom":sQuery(id+"F19.wireOp",EDGE,"E59.bottom")}),1.0]])]});
            var Q1;
            Q1=makeQuery(id+"F19.imprint","IMPRINT",FACE,{"disambiguationData":[TD([[makeQuery(id+"F19.imprint","IMPRINT",EDGE,{"derivedFrom":sQuery(id+"F19.wireOp",EDGE,"E61.1.0.0")}),1.0]])]});
            var Q2;
            Q2=makeQuery(id+"F19.imprint","IMPRINT",FACE,{"disambiguationData":[TD([[makeQuery(id+"F19.imprint","IMPRINT",EDGE,{"derivedFrom":sQuery(id+"F19.wireOp",EDGE,"E61.2.0.0")}),1.0]])]});
            var Q3;
            Q3=makeQuery(id+"F19.imprint","IMPRINT",FACE,{"disambiguationData":[TD([[makeQuery(id+"F19.imprint","IMPRINT",EDGE,{"derivedFrom":sQuery(id+"F19.wireOp",EDGE,"E62.0.3.0")}),1.0]])]});
            var Q4;
            Q4=makeQuery(id+"F19.imprint","IMPRINT",FACE,{"disambiguationData":[TD([[makeQuery(id+"F19.imprint","IMPRINT",EDGE,{"derivedFrom":sQuery(id+"F19.wireOp",EDGE,"E62.0.4.0")}),1.0]])]});
            var Q5;
            Q5=makeQuery(id+"F19.imprint","IMPRINT",FACE,{"disambiguationData":[TD([[makeQuery(id+"F19.imprint","IMPRINT",EDGE,{"derivedFrom":sQuery(id+"F19.wireOp",EDGE,"E62.0.5.0")}),1.0]])]});
            var Q6;
            Q6=makeQuery(id+"F19.imprint","IMPRINT",FACE,{"disambiguationData":[TD([[makeQuery(id+"F19.imprint","IMPRINT",EDGE,{"derivedFrom":sQuery(id+"F19.wireOp",EDGE,"E62.0.6.0")}),1.0]])]});
            var Q7;
            Q7=makeQuery(id+"F19.imprint","IMPRINT",FACE,{"disambiguationData":[TD([[makeQuery(id+"F19.imprint","IMPRINT",EDGE,{"derivedFrom":sQuery(id+"F19.wireOp",EDGE,"E62.0.7.0")}),1.0]])]});
            var Q8;
            Q8=makeQuery(id+"F19.imprint","IMPRINT",FACE,{"disambiguationData":[TD([[makeQuery(id+"F19.imprint","IMPRINT",EDGE,{"derivedFrom":sQuery(id+"F19.wireOp",EDGE,"E62.0.8.0")}),1.0]])]});
            var Q9;
            Q9=makeQuery(id+"F19.imprint","IMPRINT",FACE,{"disambiguationData":[TD([[makeQuery(id+"F19.imprint","IMPRINT",EDGE,{"derivedFrom":sQuery(id+"F19.wireOp",EDGE,"E62.0.9.0")}),1.0]])]});
            var Q10;
            Q10=makeQuery(id+"F19.imprint","IMPRINT",FACE,{"disambiguationData":[TD([[makeQuery(id+"F19.imprint","IMPRINT",EDGE,{"derivedFrom":sQuery(id+"F19.wireOp",EDGE,"E62.0.10.0")}),1.0]])]});
            var Q11;
            Q11=makeQuery(id+"F19.imprint","IMPRINT",FACE,{"disambiguationData":[TD([[makeQuery(id+"F19.imprint","IMPRINT",EDGE,{"derivedFrom":sQuery(id+"F19.wireOp",EDGE,"E62.0.11.0")}),1.0]])]});
            extrude(context, id + "F20", {"entities" : qUnion([Q0, Q1, Q2, Q3, Q4, Q5, Q6, Q7, Q8, Q9, Q10, Q11]), "operationType" : NewBodyOperationType.REMOVE, "endBound" : BoundingType.UP_TO_NEXT, "oppositeDirection" : true, "depth" : 25 * mm, "offsetDistance" : 25 * mm});
        }
        {
            var Q0;
            Q0=makeQuery(id+"F1.opExtrude","CAP_FACE",FACE,{"disambiguationData":[OSD([sQuery(id+"F0.wireOp",EDGE,"E8.0"),sQuery(id+"F0.wireOp",EDGE,"E8.1"),sQuery(id+"F0.wireOp",EDGE,"E8.2"),sQuery(id+"F0.wireOp",EDGE,"E8.3")])],"isStart":false});
            var sketch = newSketch(context, id + "F21", { "sketchPlane" : qUnion([Q0])});
            skLineSegment(sketch, "E63.bottom", {"start": v(-21.5, 5) * mm, "end": v(-29.5, 4) * mm});
            skLineSegment(sketch, "E63.top", {"start": v(-21.5, -5) * mm, "end": v(-29.5, -4) * mm});
            skLineSegment(sketch, "E63.left", {"start": v(-21.5, 5) * mm, "end": v(-21.5, -5) * mm});
            skLineSegment(sketch, "E63.right", {"start": v(-29.5, 4) * mm, "end": v(-29.5, -4) * mm});
            skLineSegment(sketch, "E64", {"start": v(0, 0) * mm, "end": v(-33.73, 0) * mm, "construction": true});
            skPoint(sketch, "E65", {"position": v(-21.5, 0) * mm});
            skCircle(sketch, "E66", {"center": v(-25.5, 0) * mm, "radius": 1.65 * mm});
            skCircle(sketch, "E67", {"center": v(-25.5, 0) * mm, "radius": 3.15 * mm, "construction": true});
            skPoint(sketch, "E68", {"position": v(-29.5, 0) * mm});
            skLineSegment(sketch, "E69.0", {"start": v(-21.5, -10) * mm, "end": v(-21.5, 48) * mm});
            skLineSegment(sketch, "E70", {"start": v(0, -10) * mm, "end": v(0, 48) * mm, "construction": true});
            skLineSegment(sketch, "E71", {"start": v(-21.5, 19) * mm, "end": v(21.5, 19) * mm, "construction": true});
            skLineSegment(sketch, "E72.MirrorCS", {"start": v(-21.5, 43) * mm, "end": v(-29.5, 42) * mm});
            skPoint(sketch, "E73.MirrorP", {"position": v(-21.5, 38) * mm});
            skCircle(sketch, "E74.MirrorC", {"center": v(-25.5, 38) * mm, "radius": 1.65 * mm});
            skLineSegment(sketch, "E75.MirrorCS", {"start": v(-21.5, 33) * mm, "end": v(-29.5, 34) * mm});
            skLineSegment(sketch, "E76.MirrorCS", {"start": v(-29.5, 34) * mm, "end": v(-29.5, 42) * mm});
            skLineSegment(sketch, "E77.MirrorCS", {"start": v(-21.5, 33) * mm, "end": v(-21.5, 43) * mm});
            skPoint(sketch, "E78.MirrorP", {"position": v(-29.5, 38) * mm});
            skCircle(sketch, "E79.MirrorC", {"center": v(-25.5, 38) * mm, "radius": 3.15 * mm, "construction": true});
            skCircle(sketch, "E80.MirrorC", {"center": v(25.5, 0) * mm, "radius": 3.15 * mm, "construction": true});
            skPoint(sketch, "E81.MirrorP", {"position": v(21.5, 0) * mm});
            skCircle(sketch, "E82.MirrorC", {"center": v(25.5, 0) * mm, "radius": 1.65 * mm});
            skLineSegment(sketch, "E83.MirrorCS", {"start": v(29.5, 4) * mm, "end": v(29.5, -4) * mm});
            skLineSegment(sketch, "E84.MirrorCS", {"start": v(21.5, 5) * mm, "end": v(21.5, -5) * mm});
            skCircle(sketch, "E85.MirrorC", {"center": v(25.5, 38) * mm, "radius": 1.65 * mm});
            skPoint(sketch, "E86.MirrorP", {"position": v(29.5, 38) * mm});
            skLineSegment(sketch, "E87.MirrorCS", {"start": v(21.5, 33) * mm, "end": v(21.5, 43) * mm});
            skLineSegment(sketch, "E88.MirrorCS", {"start": v(29.5, 34) * mm, "end": v(29.5, 42) * mm});
            skLineSegment(sketch, "E89.MirrorCS", {"start": v(21.5, 5) * mm, "end": v(29.5, 4) * mm});
            skPoint(sketch, "E90.MirrorP", {"position": v(21.5, 38) * mm});
            skCircle(sketch, "E91.MirrorC", {"center": v(25.5, 38) * mm, "radius": 3.15 * mm, "construction": true});
            skLineSegment(sketch, "E92.MirrorCS", {"start": v(21.5, -5) * mm, "end": v(29.5, -4) * mm});
            skLineSegment(sketch, "E93.MirrorCS", {"start": v(21.5, 33) * mm, "end": v(29.5, 34) * mm});
            skLineSegment(sketch, "E94.MirrorCS", {"start": v(21.5, 43) * mm, "end": v(29.5, 42) * mm});
            skPoint(sketch, "E95.MirrorP", {"position": v(29.5, 0) * mm});
            skSolve(sketch);
        }
        {
            var Q0;
            Q0=makeQuery(id+"F21.imprint","IMPRINT",FACE,{"disambiguationData":[TD([[makeQuery(id+"F21.imprint","IMPRINT",EDGE,{"derivedFrom":sQuery(id+"F21.wireOp",EDGE,"E72.MirrorCS")}),1.0]])]});
            var Q1;
            {var subQ1=sQuery(id+"F21.wireOp",EDGE,"E63.bottom");Q1=makeQuery(id+"F21.imprint","IMPRINT",FACE,{"disambiguationData":[TD([[makeQuery(id+"F21.imprint","IMPRINT",EDGE,{"derivedFrom":subQ1}),1.0]])]});}
            var Q2;
            Q2=makeQuery(id+"F21.imprint","IMPRINT",FACE,{"disambiguationData":[TD([[makeQuery(id+"F21.imprint","IMPRINT",EDGE,{"derivedFrom":sQuery(id+"F21.wireOp",EDGE,"E85.MirrorC")}),-1.0]])]});
            var Q3;
            Q3=makeQuery(id+"F21.imprint","IMPRINT",FACE,{"disambiguationData":[TD([[makeQuery(id+"F21.imprint","IMPRINT",EDGE,{"derivedFrom":sQuery(id+"F21.wireOp",EDGE,"E82.MirrorC")}),1.0]])]});
            extrude(context, id + "F22", {"entities" : qUnion([Q0, Q1, Q2, Q3]), "operationType" : NewBodyOperationType.ADD, "oppositeDirection" : true, "depth" : 2 * mm, "offsetDistance" : 25 * mm});
        }
        {
            var Q0;
            {var subQ0=sQuery(id+"F0.wireOp",EDGE,"E8.3");var subQ1=sQuery(id+"F21.wireOp",EDGE,"E89.MirrorCS");Q0=makeQuery(id+"F22.boolean.opBoolean","SPLIT",EDGE,{"disambiguationData":[TD([makeQuery(id+"F22.opExtrude","SWEPT_FACE",FACE,{"disambiguationData":[OSD([subQ1])]})])],"derivedFrom":makeQuery(id+"F1.opExtrude","CAP_EDGE",EDGE,{"disambiguationData":[OSD([subQ0])],"isStart":false})});}
            var Q1;
            Q1=makeQuery(id+"F22.opExtrude","CAP_EDGE",EDGE,{"disambiguationData":[OSD([sQuery(id+"F21.wireOp",EDGE,"E93.MirrorCS")])],"isStart":true});
            var Q2;
            Q2=makeQuery(id+"F22.opExtrude","CAP_EDGE",EDGE,{"disambiguationData":[OSD([sQuery(id+"F21.wireOp",EDGE,"E88.MirrorCS")])],"isStart":true});
            var Q3;
            Q3=makeQuery(id+"F22.opExtrude","CAP_EDGE",EDGE,{"disambiguationData":[OSD([sQuery(id+"F21.wireOp",EDGE,"E94.MirrorCS")])],"isStart":true});
            var Q4;
            {var subQ0=sQuery(id+"F0.wireOp",EDGE,"E8.0");var subQ1=sQuery(id+"F0.wireOp",EDGE,"E8.3");Q4=makeQuery(id+"F22.boolean.opBoolean","SPLIT",EDGE,{"disambiguationData":[TD([makeQuery(id+"F1.opExtrude","SWEPT_FACE",FACE,{"disambiguationData":[OSD([subQ0])]})])],"derivedFrom":makeQuery(id+"F1.opExtrude","CAP_EDGE",EDGE,{"disambiguationData":[OSD([subQ1])],"isStart":false})});}
            var Q5;
            Q5=makeQuery(id+"F1.opExtrude","CAP_EDGE",EDGE,{"disambiguationData":[OSD([sQuery(id+"F0.wireOp",EDGE,"E8.0")])],"isStart":false});
            var Q6;
            {var subQ0=sQuery(id+"F0.wireOp",EDGE,"E8.1");var subQ1=sQuery(id+"F0.wireOp",EDGE,"E8.0");Q6=makeQuery(id+"F22.boolean.opBoolean","SPLIT",EDGE,{"disambiguationData":[TD([makeQuery(id+"F1.opExtrude","SWEPT_FACE",FACE,{"disambiguationData":[OSD([subQ1])]})])],"derivedFrom":makeQuery(id+"F1.opExtrude","CAP_EDGE",EDGE,{"disambiguationData":[OSD([subQ0])],"isStart":false})});}
            var Q7;
            Q7=makeQuery(id+"F22.opExtrude","CAP_EDGE",EDGE,{"disambiguationData":[OSD([sQuery(id+"F21.wireOp",EDGE,"E72.MirrorCS")])],"isStart":true});
            var Q8;
            Q8=makeQuery(id+"F22.opExtrude","CAP_EDGE",EDGE,{"disambiguationData":[OSD([sQuery(id+"F21.wireOp",EDGE,"E76.MirrorCS")])],"isStart":true});
            var Q9;
            Q9=makeQuery(id+"F22.opExtrude","CAP_EDGE",EDGE,{"disambiguationData":[OSD([sQuery(id+"F21.wireOp",EDGE,"E75.MirrorCS")])],"isStart":true});
            var Q10;
            {var subQ0=sQuery(id+"F21.wireOp",EDGE,"E63.bottom");var subQ1=sQuery(id+"F0.wireOp",EDGE,"E8.1");Q10=makeQuery(id+"F22.boolean.opBoolean","SPLIT",EDGE,{"disambiguationData":[TD([makeQuery(id+"F22.opExtrude","SWEPT_FACE",FACE,{"disambiguationData":[OSD([subQ0])]})])],"derivedFrom":makeQuery(id+"F1.opExtrude","CAP_EDGE",EDGE,{"disambiguationData":[OSD([subQ1])],"isStart":false})});}
            var Q11;
            Q11=makeQuery(id+"F22.opExtrude","CAP_EDGE",EDGE,{"disambiguationData":[OSD([sQuery(id+"F21.wireOp",EDGE,"E63.bottom")])],"isStart":true});
            var Q12;
            Q12=makeQuery(id+"F22.opExtrude","CAP_EDGE",EDGE,{"disambiguationData":[OSD([sQuery(id+"F21.wireOp",EDGE,"E63.right")])],"isStart":true});
            var Q13;
            Q13=makeQuery(id+"F22.opExtrude","CAP_EDGE",EDGE,{"disambiguationData":[OSD([sQuery(id+"F21.wireOp",EDGE,"E63.top")])],"isStart":true});
            var Q14;
            {var subQ0=sQuery(id+"F0.wireOp",EDGE,"E8.2");var subQ1=sQuery(id+"F0.wireOp",EDGE,"E8.1");Q14=makeQuery(id+"F22.boolean.opBoolean","SPLIT",EDGE,{"disambiguationData":[TD([makeQuery(id+"F1.opExtrude","SWEPT_FACE",FACE,{"disambiguationData":[OSD([subQ0])]})])],"derivedFrom":makeQuery(id+"F1.opExtrude","CAP_EDGE",EDGE,{"disambiguationData":[OSD([subQ1])],"isStart":false})});}
            var Q15;
            Q15=makeQuery(id+"F1.opExtrude","CAP_EDGE",EDGE,{"disambiguationData":[OSD([sQuery(id+"F0.wireOp",EDGE,"E8.2")])],"isStart":false});
            var Q16;
            {var subQ0=sQuery(id+"F0.wireOp",EDGE,"E8.3");var subQ1=sQuery(id+"F0.wireOp",EDGE,"E8.2");Q16=makeQuery(id+"F22.boolean.opBoolean","SPLIT",EDGE,{"disambiguationData":[TD([makeQuery(id+"F1.opExtrude","SWEPT_FACE",FACE,{"disambiguationData":[OSD([subQ1])]})])],"derivedFrom":makeQuery(id+"F1.opExtrude","CAP_EDGE",EDGE,{"disambiguationData":[OSD([subQ0])],"isStart":false})});}
            var Q17;
            Q17=makeQuery(id+"F22.opExtrude","CAP_EDGE",EDGE,{"disambiguationData":[OSD([sQuery(id+"F21.wireOp",EDGE,"E92.MirrorCS")])],"isStart":true});
            var Q18;
            Q18=makeQuery(id+"F22.opExtrude","CAP_EDGE",EDGE,{"disambiguationData":[OSD([sQuery(id+"F21.wireOp",EDGE,"E83.MirrorCS")])],"isStart":true});
            var Q19;
            Q19=makeQuery(id+"F22.opExtrude","CAP_EDGE",EDGE,{"disambiguationData":[OSD([sQuery(id+"F21.wireOp",EDGE,"E89.MirrorCS")])],"isStart":true});
            var Q20;
            Q20=makeQuery(id+"F10.opExtrude","CAP_EDGE",EDGE,{"disambiguationData":[OSD([sQuery(id+"F9.wireOp",EDGE,"E20.0")])],"isStart":false});
            chamfer(context, id + "F23", {"entities" : qUnion([Q0, Q1, Q2, Q3, Q4, Q5, Q6, Q7, Q8, Q9, Q10, Q11, Q12, Q13, Q14, Q15, Q16, Q17, Q18, Q19, Q20]), "width" : 0.5 * mm, "tangentPropagation" : true});
        }
        {
            var Q0;
            Q0=makeQuery(id+"F10.opExtrude","CAP_EDGE",EDGE,{"disambiguationData":[OSD([sQuery(id+"F9.wireOp",EDGE,"E21.0")])],"isStart":false});
            var Q1;
            Q1=makeQuery(id+"F10.opExtrude","CAP_EDGE",EDGE,{"disambiguationData":[OSD([sQuery(id+"F9.wireOp",EDGE,"E18.0")])],"isStart":false});
            var Q2;
            Q2=makeQuery(id+"F10.opExtrude","CAP_EDGE",EDGE,{"disambiguationData":[OSD([sQuery(id+"F9.wireOp",EDGE,"E19.0")])],"isStart":false});
            chamfer(context, id + "F24", {"entities" : qUnion([Q0, Q1, Q2]), "width" : 0.5 * mm, "tangentPropagation" : true});
        }
    });
